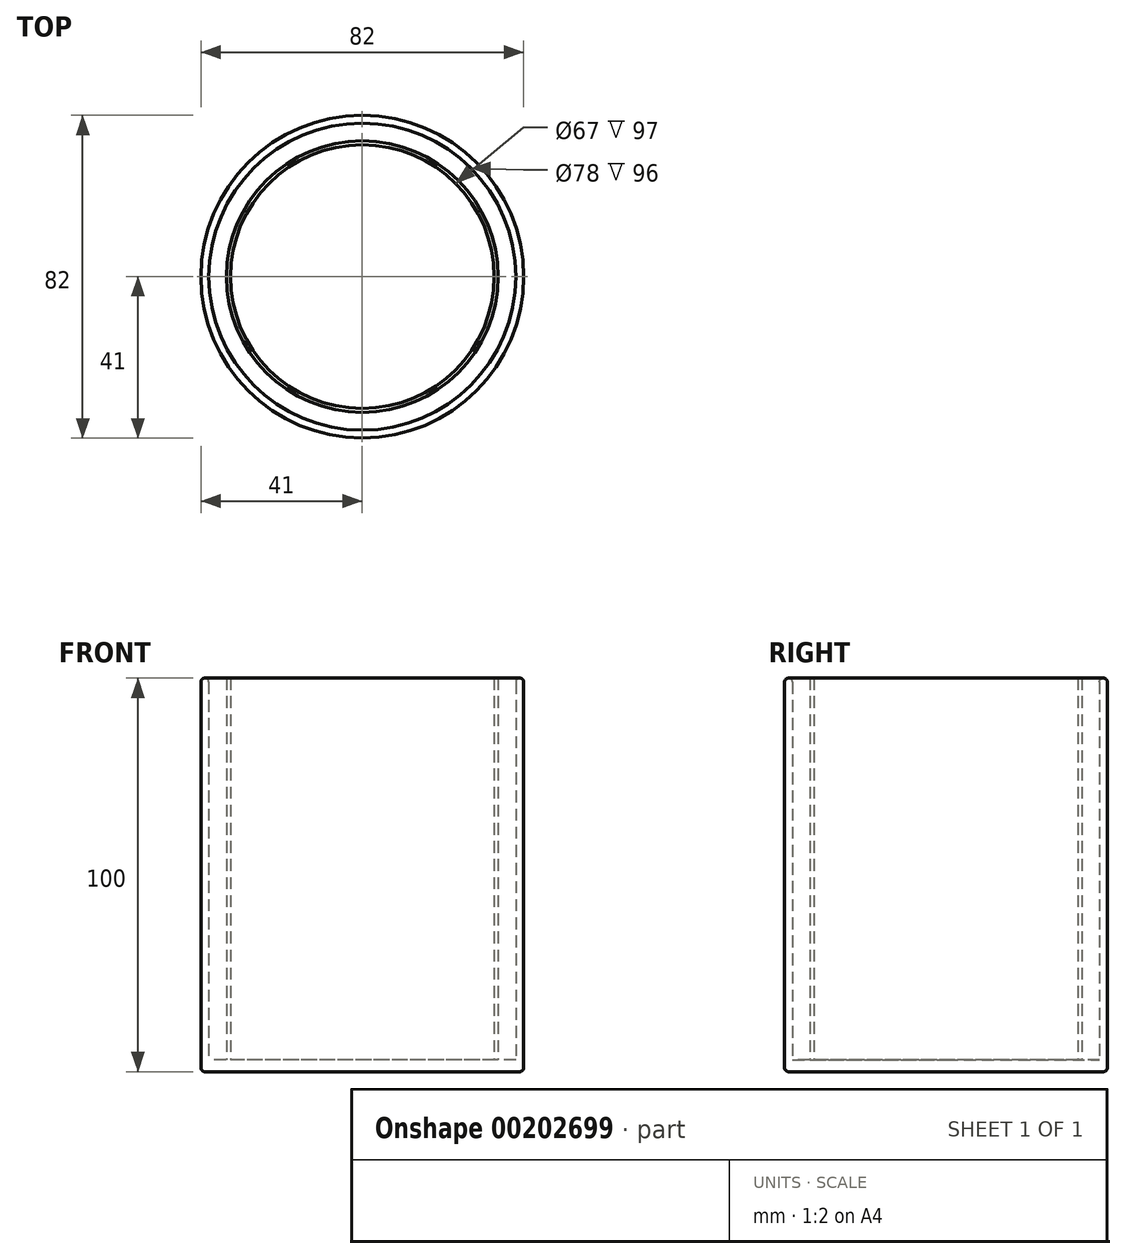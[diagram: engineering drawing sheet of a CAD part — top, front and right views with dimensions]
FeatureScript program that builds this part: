
annotation { "Feature Type Name" : "Feature", "Feature Type Description" : "" }
export const myFeature = defineFeature(function(context is Context, id is Id, definition is map)
    precondition{}
    {
        {
            var Q0;
            Q0=qCreatedBy(makeId("Top.planeOp"),FACE);
            var sketch = newSketch(context, id + "F0", { "sketchPlane" : qUnion([Q0])});
            skCircle(sketch, "E0", {"center": v(0, 0) * mm, "radius": 33.5 * mm});
            skSolve(sketch);
        }
        {
            var Q0;
            Q0 = qSketchRegion(id + "F0", true);
            extrude(context, id + "F1", {"entities" : qUnion([Q0]), "depth" : 3 * mm});
        }
        {
            var Q0;
            Q0=qCreatedBy(makeId("Top.planeOp"),FACE);
            var sketch = newSketch(context, id + "F2", { "sketchPlane" : qUnion([Q0])});
            skCircle(sketch, "E1", {"center": v(0, 0) * mm, "radius": 33.5 * mm});
            skCircle(sketch, "E2", {"center": v(0, 0) * mm, "radius": 34.5 * mm});
            skSolve(sketch);
        }
        {
            var Q0;
            Q0 = qSketchRegion(id + "F2", true);
            extrude(context, id + "F3", {"entities" : qUnion([Q0]), "operationType" : NewBodyOperationType.ADD, "depth" : 100 * mm});
        }
        {
            var Q0;
            Q0=qCreatedBy(makeId("Top.planeOp"),FACE);
            var sketch = newSketch(context, id + "F4", { "sketchPlane" : qUnion([Q0])});
            skCircle(sketch, "E3", {"center": v(0, 0) * mm, "radius": 41 * mm});
            skSolve(sketch);
        }
        {
            var Q0;
            Q0 = qSketchRegion(id + "F4", true);
            extrude(context, id + "F5", {"entities" : qUnion([Q0]), "operationType" : NewBodyOperationType.ADD, "depth" : 3 * mm});
        }
        {
            var Q0;
            Q0=qCreatedBy(makeId("Top.planeOp"),FACE);
            var sketch = newSketch(context, id + "F6", { "sketchPlane" : qUnion([Q0])});
            skCircle(sketch, "E4", {"center": v(0, 0) * mm, "radius": 39 * mm});
            skCircle(sketch, "E5", {"center": v(0, 0) * mm, "radius": 41 * mm});
            skSolve(sketch);
        }
        {
            var Q0;
            Q0 = qSketchRegion(id + "F6", true);
            extrude(context, id + "F7", {"entities" : qUnion([Q0]), "operationType" : NewBodyOperationType.ADD, "depth" : 100 * mm});
        }
        {
            var Q0;
            Q0=makeQuery(id+"F5.boolean.opBoolean","MERGE",FACE,{"derivedFrom":[makeQuery(id+"F3.boolean.opBoolean","MERGE",FACE,{"derivedFrom":[makeQuery(id+"F1.opExtrude","CAP_FACE",FACE,{"disambiguationData":[OSD([sQuery(id+"F0.wireOp",EDGE,"E0")])],"isStart":true}),makeQuery(id+"F3.opExtrude","CAP_FACE",FACE,{"disambiguationData":[OSD([sQuery(id+"F2.wireOp",EDGE,"E1"),sQuery(id+"F2.wireOp",EDGE,"E2")])],"isStart":true})]}),makeQuery(id+"F5.opExtrude","CAP_FACE",FACE,{"disambiguationData":[OSD([sQuery(id+"F4.wireOp",EDGE,"E3")])],"isStart":true})]});
            fillet(context, id + "F8", {"entities" : qUnion([Q0]), "radius" : 1 * mm, "tangentPropagation" : true, "allowEdgeOverflow" : false});
        }
        {
            var Q0;
            Q0=makeQuery(id+"F7.opExtrude","CAP_EDGE",EDGE,{"disambiguationData":[OSD([sQuery(id+"F6.wireOp",EDGE,"E5")])],"isStart":false});
            var Q1;
            Q1=makeQuery(id+"F7.opExtrude","CAP_FACE",FACE,{"disambiguationData":[OSD([sQuery(id+"F6.wireOp",EDGE,"E4"),sQuery(id+"F6.wireOp",EDGE,"E5")])],"isStart":false});
            fillet(context, id + "F9", {"entities" : qUnion([Q0, Q1]), "radius" : 1 * mm, "tangentPropagation" : true, "allowEdgeOverflow" : false});
        }
    });
